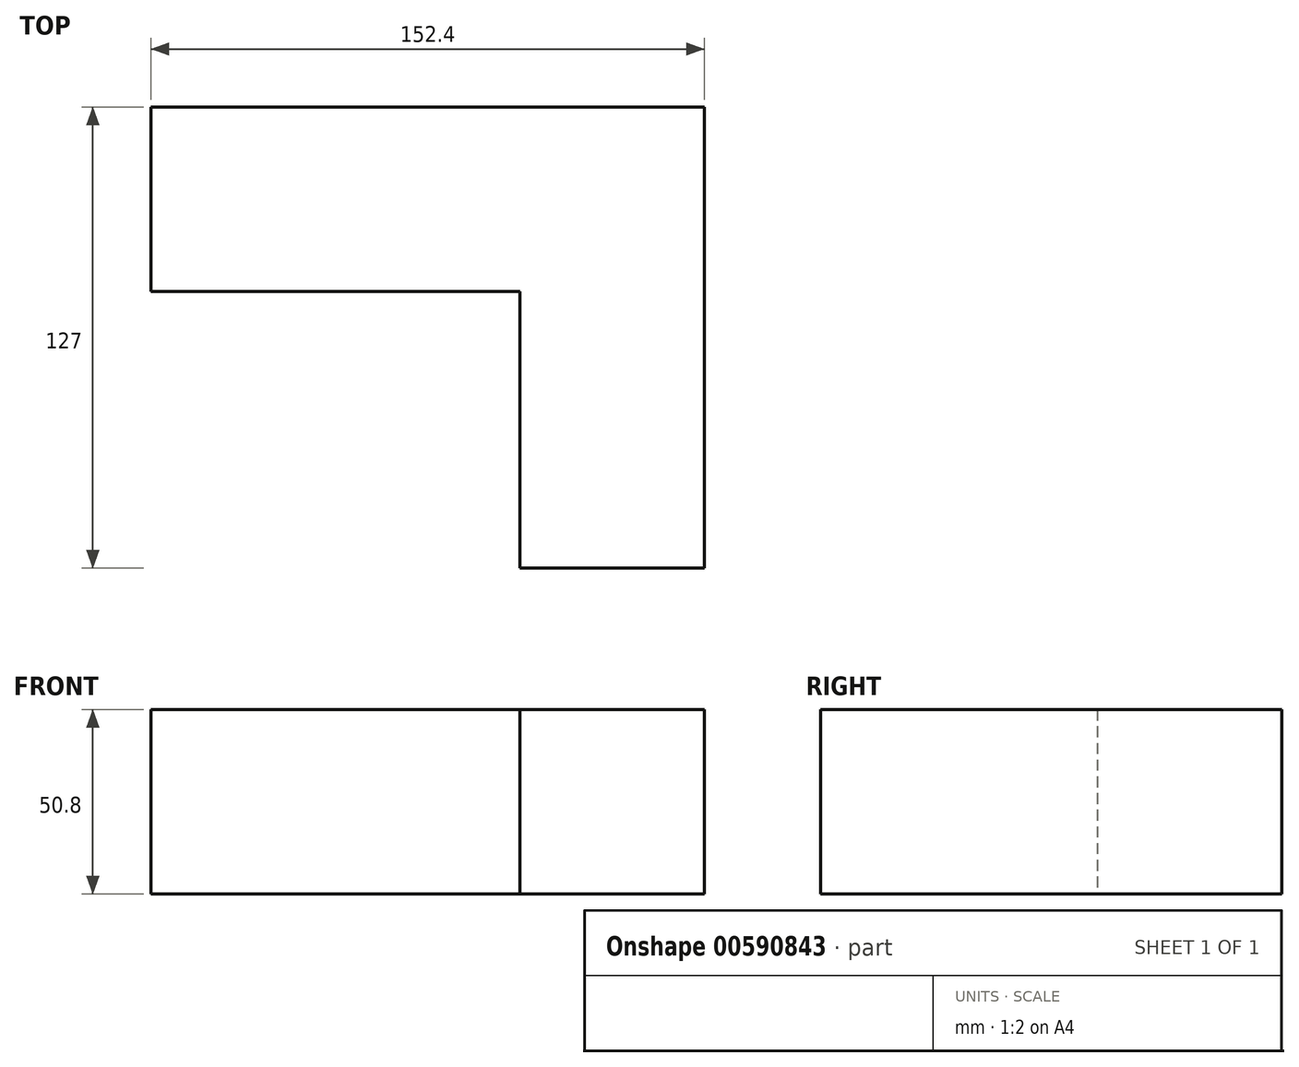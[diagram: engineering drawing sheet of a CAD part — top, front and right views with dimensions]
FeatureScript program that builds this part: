
annotation { "Feature Type Name" : "Feature", "Feature Type Description" : "" }
export const myFeature = defineFeature(function(context is Context, id is Id, definition is map)
    precondition{}
    {
        {
            var Q0;
            Q0=qCreatedBy(makeId("Top.planeOp"),FACE);
            var sketch = newSketch(context, id + "F0", { "sketchPlane" : qUnion([Q0])});
            skLineSegment(sketch, "E0", {"start": v(-78.78, 37.4) * mm, "end": v(73.62, 37.4) * mm});
            skLineSegment(sketch, "E1", {"start": v(73.62, 37.4) * mm, "end": v(73.62, -89.6) * mm});
            skLineSegment(sketch, "E2", {"start": v(73.62, -89.6) * mm, "end": v(22.82, -89.6) * mm});
            skLineSegment(sketch, "E3", {"start": v(22.82, -89.6) * mm, "end": v(22.82, -13.4) * mm});
            skLineSegment(sketch, "E4", {"start": v(22.82, -13.4) * mm, "end": v(-78.78, -13.4) * mm});
            skLineSegment(sketch, "E5", {"start": v(-78.78, -13.4) * mm, "end": v(-78.78, 37.4) * mm});
            skSolve(sketch);
        }
        {
            var Q0;
            Q0=makeQuery(id+"F0.imprint","IMPRINT",FACE,{"disambiguationData":[TD([[makeQuery(id+"F0.imprint","IMPRINT",EDGE,{"derivedFrom":sQuery(id+"F0.wireOp",EDGE,"E0")}),-1.0]])]});
            extrude(context, id + "F1", {"entities" : qUnion([Q0]), "depth" : 50.8 * mm, "offsetDistance" : 25.4 * mm});
        }
    });
